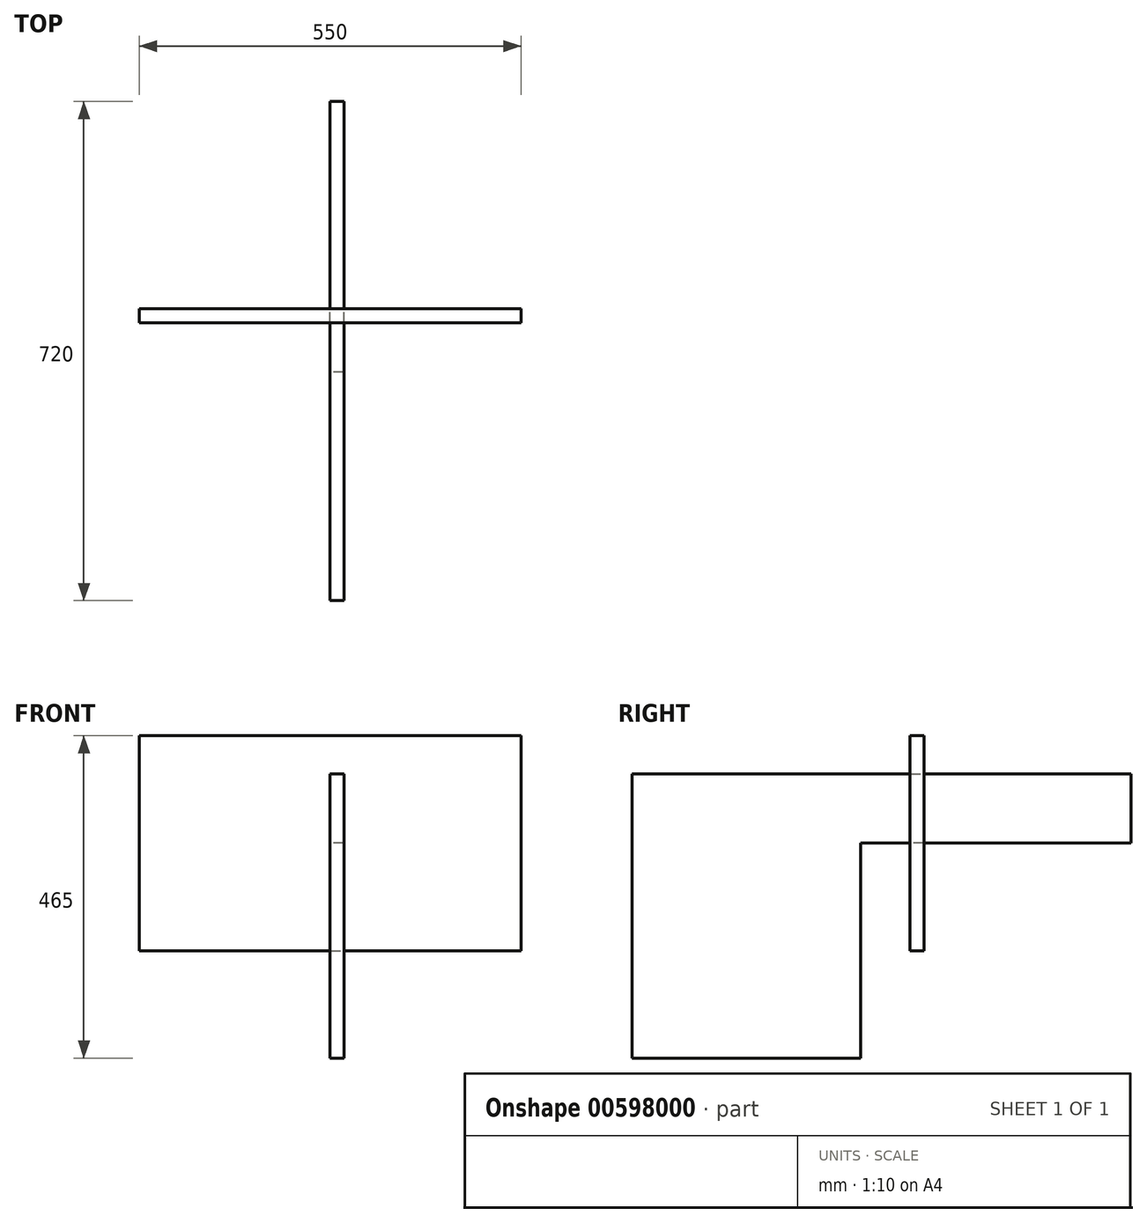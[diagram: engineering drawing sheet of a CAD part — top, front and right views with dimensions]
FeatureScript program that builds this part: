
annotation { "Feature Type Name" : "Feature", "Feature Type Description" : "" }
export const myFeature = defineFeature(function(context is Context, id is Id, definition is map)
    precondition{}
    {
        {
            var Q0;
            Q0=qCreatedBy(makeId("Right.planeOp"),FACE);
            var sketch = newSketch(context, id + "F0", { "sketchPlane" : qUnion([Q0])});
            skLineSegment(sketch, "E0", {"start": v(-421.04, 100) * mm, "end": v(298.96, 100) * mm});
            skLineSegment(sketch, "E1", {"start": v(298.96, 100) * mm, "end": v(298.96, 0) * mm});
            skLineSegment(sketch, "E2", {"start": v(298.96, 0) * mm, "end": v(-91.04, 0) * mm});
            skLineSegment(sketch, "E3", {"start": v(-91.04, 0) * mm, "end": v(-91.04, -310) * mm});
            skLineSegment(sketch, "E4", {"start": v(-91.04, -310) * mm, "end": v(-421.04, -310) * mm});
            skLineSegment(sketch, "E5", {"start": v(-421.04, -310) * mm, "end": v(-421.04, 100) * mm});
            skSolve(sketch);
        }
        {
            var Q0;
            Q0 = qSketchRegion(id + "F0", true);
            extrude(context, id + "F1", {"entities" : qUnion([Q0]), "depth" : 20 * mm, "offsetDistance" : 25 * mm});
        }
        {
            var Q0;
            Q0=qCreatedBy(makeId("Front.planeOp"),FACE);
            var sketch = newSketch(context, id + "F2", { "sketchPlane" : qUnion([Q0])});
            skLineSegment(sketch, "E6.bottom", {"start": v(-275, -155) * mm, "end": v(275, -155) * mm});
            skLineSegment(sketch, "E6.top", {"start": v(-275, 155) * mm, "end": v(275, 155) * mm});
            skLineSegment(sketch, "E6.left", {"start": v(-275, -155) * mm, "end": v(-275, 155) * mm});
            skLineSegment(sketch, "E6.right", {"start": v(275, -155) * mm, "end": v(275, 155) * mm});
            skPoint(sketch, "E6.middle", {"position": v(0, 0) * mm});
            skSolve(sketch);
        }
        {
            var Q0;
            Q0=makeQuery(id+"F2.imprint","IMPRINT",FACE,{"disambiguationData":[TD([[makeQuery(id+"F2.imprint","IMPRINT",EDGE,{"derivedFrom":sQuery(id+"F2.wireOp",EDGE,"E6.bottom")}),1.0]])]});
            extrude(context, id + "F3", {"entities" : qUnion([Q0]), "depth" : 20 * mm, "offsetDistance" : 25 * mm});
        }
    });
